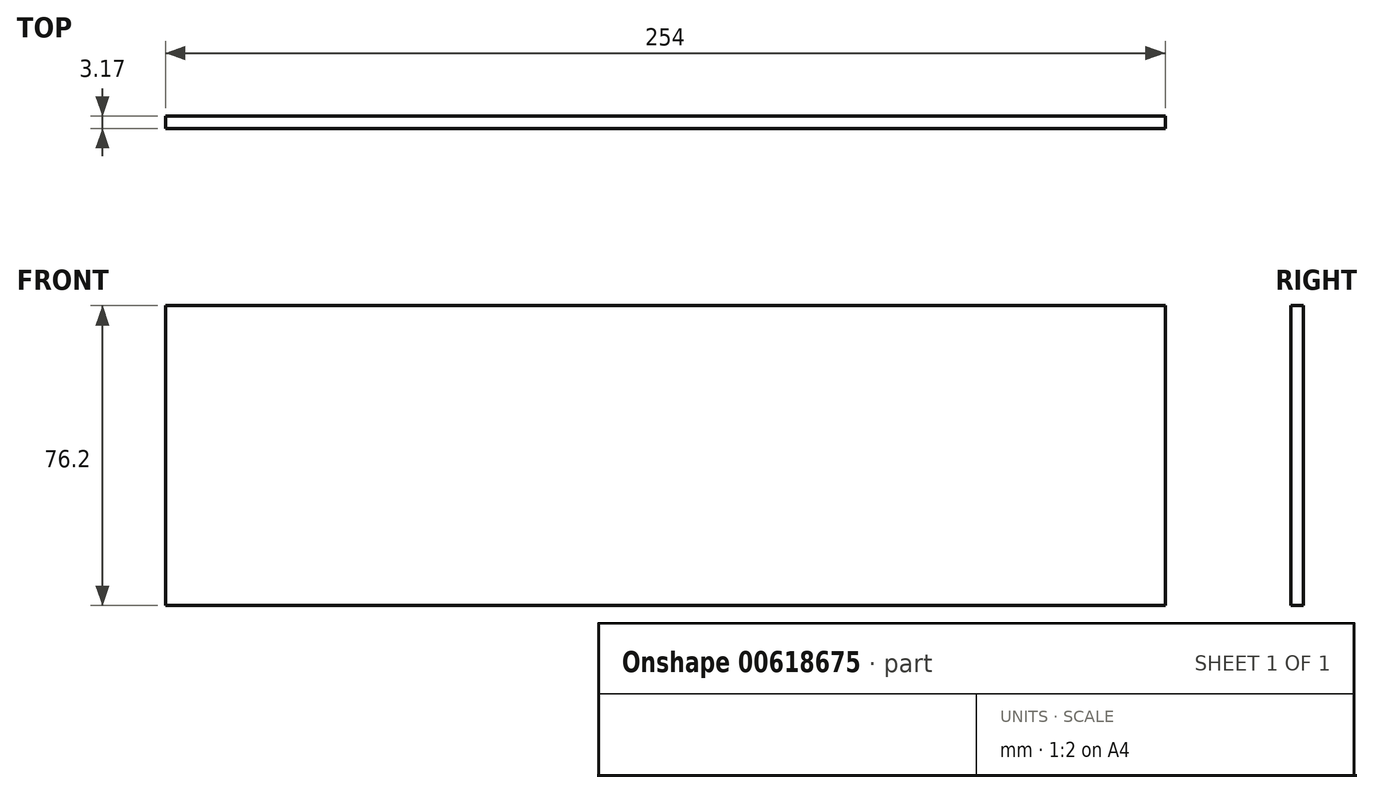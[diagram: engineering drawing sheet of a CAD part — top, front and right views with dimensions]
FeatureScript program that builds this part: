
annotation { "Feature Type Name" : "Feature", "Feature Type Description" : "" }
export const myFeature = defineFeature(function(context is Context, id is Id, definition is map)
    precondition{}
    {
        {
            var Q0;
            Q0=qCreatedBy(makeId("Front.planeOp"),FACE);
            var sketch = newSketch(context, id + "F0", { "sketchPlane" : qUnion([Q0])});
            skLineSegment(sketch, "E0.bottom", {"start": v(127, 38.1) * mm, "end": v(-127, 38.1) * mm});
            skLineSegment(sketch, "E0.top", {"start": v(127, -38.1) * mm, "end": v(-127, -38.1) * mm});
            skLineSegment(sketch, "E0.left", {"start": v(127, 38.1) * mm, "end": v(127, -38.1) * mm});
            skLineSegment(sketch, "E0.right", {"start": v(-127, 38.1) * mm, "end": v(-127, -38.1) * mm});
            skPoint(sketch, "E0.middle", {"position": v(0, 0) * mm});
            skSolve(sketch);
        }
        {
            var Q0;
            Q0 = qSketchRegion(id + "F0", true);
            extrude(context, id + "F1", {"entities" : qUnion([Q0]), "depth" : 3.17 * mm, "offsetDistance" : 25.4 * mm});
        }
    });
